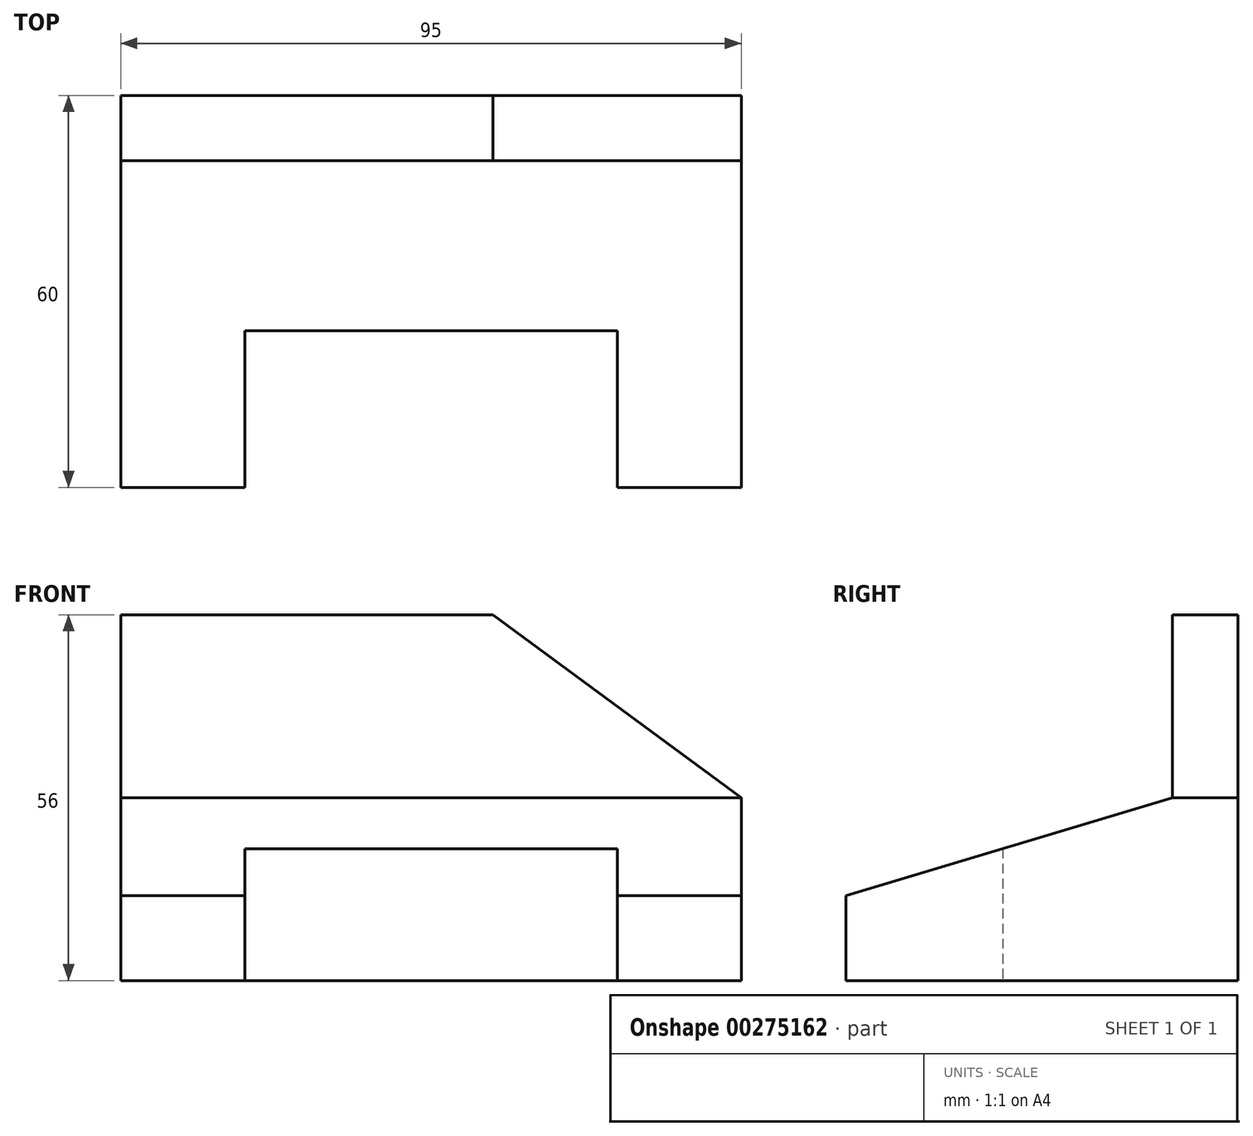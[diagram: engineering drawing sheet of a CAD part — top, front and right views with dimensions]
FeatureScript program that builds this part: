
annotation { "Feature Type Name" : "Feature", "Feature Type Description" : "" }
export const myFeature = defineFeature(function(context is Context, id is Id, definition is map)
    precondition{}
    {
        {
            var Q0;
            Q0=qCreatedBy(makeId("Right.planeOp"),FACE);
            var sketch = newSketch(context, id + "F0", { "sketchPlane" : qUnion([Q0])});
            skLineSegment(sketch, "E0", {"start": v(-10, 56) * mm, "end": v(0, 56) * mm});
            skLineSegment(sketch, "E1", {"start": v(0, 56) * mm, "end": v(0, 0) * mm});
            skLineSegment(sketch, "E2", {"start": v(0, 0) * mm, "end": v(-60, 0) * mm});
            skLineSegment(sketch, "E3", {"start": v(-60, 0) * mm, "end": v(-60, 13) * mm});
            skLineSegment(sketch, "E4", {"start": v(-60, 13) * mm, "end": v(-10, 28) * mm});
            skLineSegment(sketch, "E5", {"start": v(-10, 28) * mm, "end": v(-10, 56) * mm});
            skSolve(sketch);
        }
        {
            var Q0;
            Q0 = qSketchRegion(id + "F0", true);
            extrude(context, id + "F1", {"entities" : qUnion([Q0]), "depth" : 95 * mm});
        }
        {
            var Q0;
            Q0=makeQuery(id+"F1.opExtrude","SWEPT_FACE",FACE,{"disambiguationData":[OSD([sQuery(id+"F0.wireOp",EDGE,"E5")])]});
            var sketch = newSketch(context, id + "F2", { "sketchPlane" : qUnion([Q0])});
            skLineSegment(sketch, "E6", {"start": v(57, 56) * mm, "end": v(95, 28) * mm});
            skSolve(sketch);
        }
        {
            var Q0;
            {var subQ0=sQuery(id+"F2.wireOp",EDGE,"E6");Q0=makeQuery(id+"F2.imprint","IMPRINT",FACE,{"disambiguationData":[TD([[makeQuery(id+"F2.imprint","IMPRINT",EDGE,{"derivedFrom":subQ0}),1.0]])]});}
            extrude(context, id + "F3", {"entities" : qUnion([Q0]), "operationType" : NewBodyOperationType.REMOVE, "endBound" : BoundingType.THROUGH_ALL, "oppositeDirection" : true, "depth" : 74.5 * mm});
        }
        {
            var Q0;
            Q0=makeQuery(id+"F1.opExtrude","SWEPT_FACE",FACE,{"disambiguationData":[OSD([sQuery(id+"F0.wireOp",EDGE,"E2")])]});
            var sketch = newSketch(context, id + "F4", { "sketchPlane" : qUnion([Q0])});
            skLineSegment(sketch, "E7.bottom", {"start": v(19, 60) * mm, "end": v(76, 60) * mm});
            skLineSegment(sketch, "E7.top", {"start": v(19, 36) * mm, "end": v(76, 36) * mm});
            skLineSegment(sketch, "E7.left", {"start": v(19, 60) * mm, "end": v(19, 36) * mm});
            skLineSegment(sketch, "E7.right", {"start": v(76, 60) * mm, "end": v(76, 36) * mm});
            skSolve(sketch);
        }
        {
            var Q0;
            Q0 = qSketchRegion(id + "F4", true);
            extrude(context, id + "F5", {"entities" : qUnion([Q0]), "operationType" : NewBodyOperationType.ADD, "endBound" : BoundingType.THROUGH_ALL, "depth" : 25 * mm});
        }
        {
            var Q0;
            Q0 = qSketchRegion(id + "F4", true);
            var Q1;
            Q1=makeQuery(id+"F5.opExtrude","CAP_FACE",FACE,{"disambiguationData":[OSD([sQuery(id+"F4.wireOp",EDGE,"E7.bottom"),sQuery(id+"F4.wireOp",EDGE,"E7.top"),sQuery(id+"F4.wireOp",EDGE,"E7.left"),sQuery(id+"F4.wireOp",EDGE,"E7.right")])],"isStart":false});
            extrude(context, id + "F6", {"entities" : qUnion([Q0, Q1]), "operationType" : NewBodyOperationType.REMOVE, "endBound" : BoundingType.THROUGH_ALL, "depth" : 25 * mm});
        }
        {
            var Q0;
            {var subQ0=sQuery(id+"F4.wireOp",EDGE,"E7.right");var subQ1=sQuery(id+"F4.wireOp",EDGE,"E7.left");var subQ2=sQuery(id+"F4.wireOp",EDGE,"E7.top");var subQ3=sQuery(id+"F4.wireOp",EDGE,"E7.bottom");Q0=makeQuery(id+"F6.boolean.opBoolean","MERGE",FACE,{"derivedFrom":[makeQuery(id+"F1.opExtrude","SWEPT_FACE",FACE,{"disambiguationData":[OSD([sQuery(id+"F0.wireOp",EDGE,"E2")])]}),makeQuery(id+"F6.opExtrude","CAP_FACE",FACE,{"disambiguationData":[OSD([subQ3,subQ2,subQ1,subQ0]),TDD([makeQuery(id+"F4.imprint","IMPRINT",EDGE,{"derivedFrom":subQ3}),makeQuery(id+"F4.imprint","IMPRINT",EDGE,{"derivedFrom":subQ2}),makeQuery(id+"F4.imprint","IMPRINT",EDGE,{"derivedFrom":subQ1}),makeQuery(id+"F4.imprint","IMPRINT",EDGE,{"derivedFrom":subQ0})])],"isStart":true})]});}
            var sketch = newSketch(context, id + "F7", { "sketchPlane" : qUnion([Q0])});
            skLineSegment(sketch, "E8.bottom", {"start": v(19, 60) * mm, "end": v(76, 60) * mm});
            skLineSegment(sketch, "E8.top", {"start": v(19, 36) * mm, "end": v(76, 36) * mm});
            skLineSegment(sketch, "E8.left", {"start": v(19, 60) * mm, "end": v(19, 36) * mm});
            skLineSegment(sketch, "E8.right", {"start": v(76, 60) * mm, "end": v(76, 36) * mm});
            skSolve(sketch);
        }
        {
            var Q0;
            Q0=makeQuery(id+"F7.imprint","IMPRINT",FACE,{"disambiguationData":[TD([[makeQuery(id+"F7.imprint","IMPRINT",EDGE,{"derivedFrom":sQuery(id+"F7.wireOp",EDGE,"E8.bottom")}),1.0]])]});
            extrude(context, id + "F8", {"entities" : qUnion([Q0]), "operationType" : NewBodyOperationType.REMOVE, "endBound" : BoundingType.THROUGH_ALL, "oppositeDirection" : true, "depth" : 25 * mm});
        }
        {
            var Q0;
            Q0=makeQuery(id+"F4.imprint","IMPRINT",FACE,{"disambiguationData":[TD([[makeQuery(id+"F4.imprint","IMPRINT",EDGE,{"derivedFrom":sQuery(id+"F4.wireOp",EDGE,"E7.bottom")}),1.0]])]});
            extrude(context, id + "F9", {"entities" : qUnion([Q0]), "operationType" : NewBodyOperationType.REMOVE, "endBound" : BoundingType.THROUGH_ALL, "depth" : 25 * mm});
        }
    });
